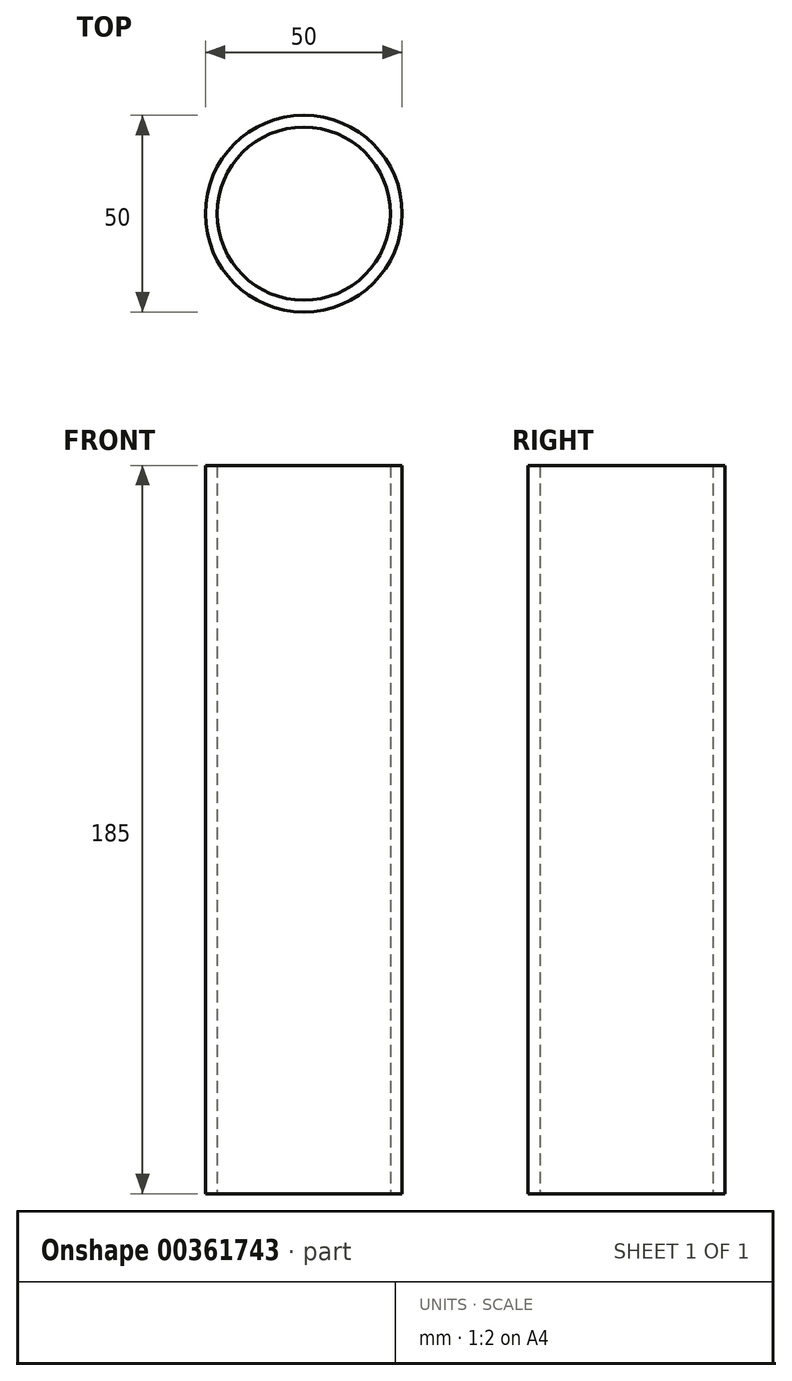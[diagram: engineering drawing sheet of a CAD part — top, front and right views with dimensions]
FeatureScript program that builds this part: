
annotation { "Feature Type Name" : "Feature", "Feature Type Description" : "" }
export const myFeature = defineFeature(function(context is Context, id is Id, definition is map)
    precondition{}
    {
        {
            var Q0;
            Q0=qCreatedBy(makeId("Top.planeOp"),FACE);
            var sketch = newSketch(context, id + "F0", { "sketchPlane" : qUnion([Q0])});
            skCircle(sketch, "E0", {"center": v(0, 0) * mm, "radius": 25 * mm});
            skCircle(sketch, "E1", {"center": v(0, 0) * mm, "radius": 22 * mm});
            skSolve(sketch);
        }
        {
            var Q0;
            Q0=makeQuery(id+"F0.imprint","IMPRINT",FACE,{"disambiguationData":[TD([[makeQuery(id+"F0.imprint","IMPRINT",EDGE,{"derivedFrom":sQuery(id+"F0.wireOp",EDGE,"E0")}),1.0]])]});
            var Q1;
            Q1=sQuery(id+"F0.wireOp",EDGE,"E0");
            var Q2;
            Q2=sQuery(id+"F0.wireOp",EDGE,"E1");
            extrude(context, id + "F1", {"entities" : qUnion([Q0]), "surfaceEntities" : qUnion([Q1, Q2]), "depth" : 185 * mm});
        }
    });
